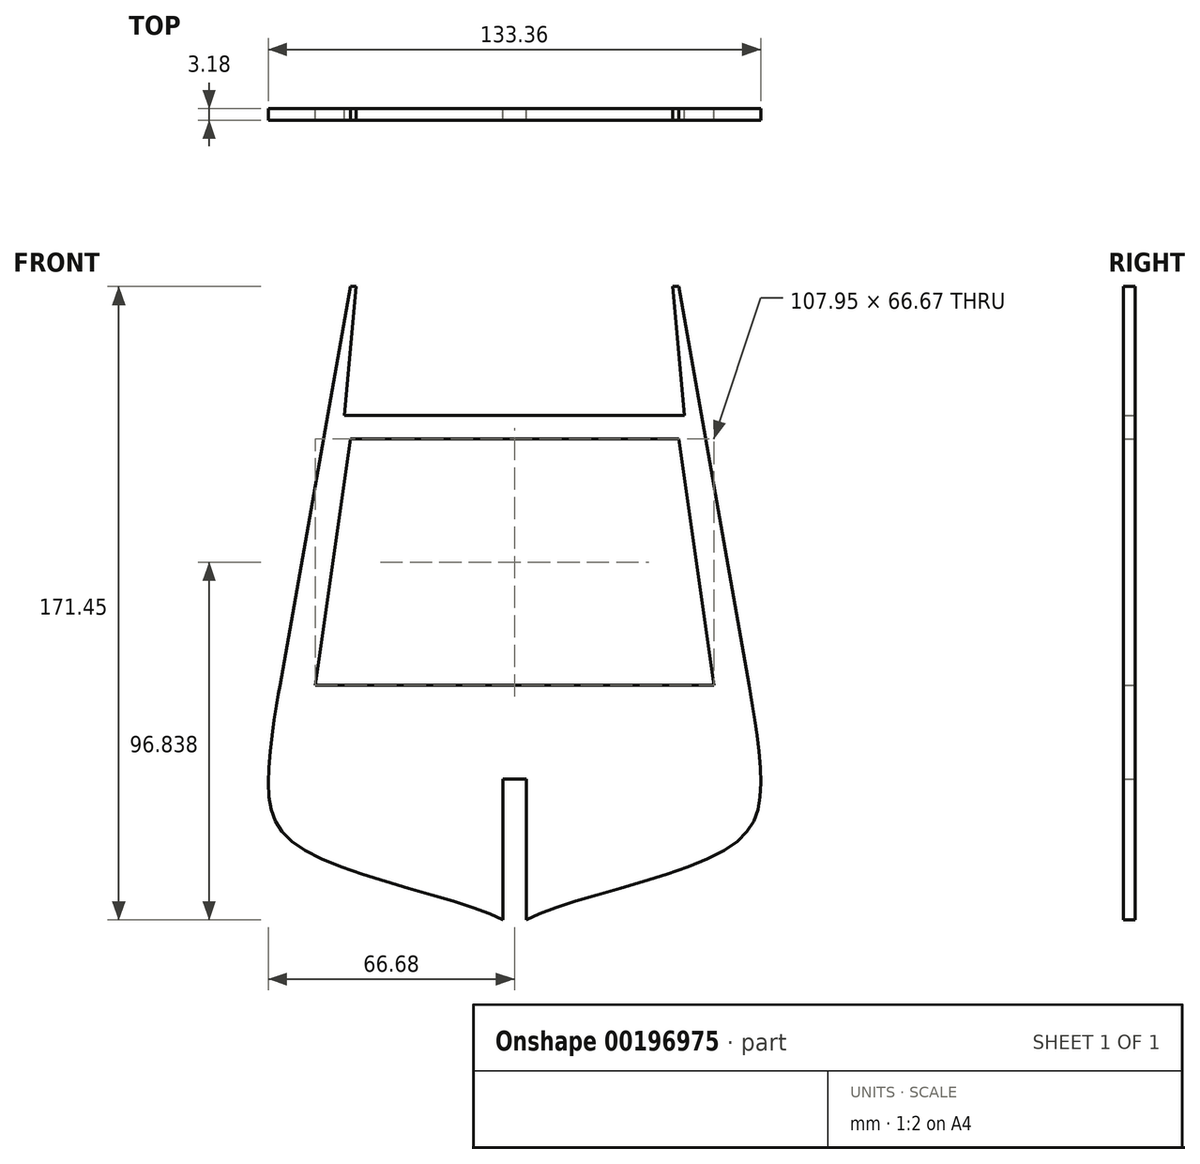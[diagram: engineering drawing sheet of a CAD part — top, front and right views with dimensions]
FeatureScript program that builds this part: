
annotation { "Feature Type Name" : "Feature", "Feature Type Description" : "" }
export const myFeature = defineFeature(function(context is Context, id is Id, definition is map)
    precondition{}
    {
        {
            var Q0;
            Q0=qCreatedBy(makeId("Front.planeOp"),FACE);
            var sketch = newSketch(context, id + "F0", { "sketchPlane" : qUnion([Q0])});
            skLineSegment(sketch, "E0", {"start": v(0, 0) * mm, "end": v(0, 66.68) * mm, "construction": true});
            skLineSegment(sketch, "E1", {"start": v(0, 0) * mm, "end": v(0, -63.5) * mm, "construction": true});
            skLineSegment(sketch, "E2", {"start": v(0, 0) * mm, "end": v(53.97, 0) * mm});
            skLineSegment(sketch, "E3", {"start": v(0, 0) * mm, "end": v(-53.97, 0) * mm});
            skLineSegment(sketch, "E4", {"start": v(53.97, 0) * mm, "end": v(63.5, 0) * mm, "construction": true});
            skLineSegment(sketch, "E5", {"start": v(0, -63.5) * mm, "end": v(3.18, -63.5) * mm, "construction": true});
            skLineSegment(sketch, "E6", {"start": v(0, 66.68) * mm, "end": v(44.45, 66.68) * mm});
            skLineSegment(sketch, "E7", {"start": v(44.45, 66.68) * mm, "end": v(51.73, 66.68) * mm, "construction": true});
            skLineSegment(sketch, "E8", {"start": v(0, 66.68) * mm, "end": v(0, 73.03) * mm, "construction": true});
            skLineSegment(sketch, "E9", {"start": v(0, 73.03) * mm, "end": v(46.04, 73.03) * mm});
            skLineSegment(sketch, "E10", {"start": v(46.04, 73.03) * mm, "end": v(50.61, 73.03) * mm, "construction": true});
            skLineSegment(sketch, "E11", {"start": v(44.45, 66.68) * mm, "end": v(53.97, 0) * mm});
            skLineSegment(sketch, "E12", {"start": v(3.18, -63.5) * mm, "end": v(3.18, -25.4) * mm});
            skLineSegment(sketch, "E13", {"start": v(-3.18, -25.4) * mm, "end": v(-3.18, -63.5) * mm});
            skLineSegment(sketch, "E14", {"start": v(-3.18, -25.4) * mm, "end": v(0, -25.4) * mm});
            skLineSegment(sketch, "E15", {"start": v(0, -25.4) * mm, "end": v(3.18, -25.4) * mm});
            skLineSegment(sketch, "E16", {"start": v(44.45, 107.95) * mm, "end": v(42.86, 107.95) * mm});
            skLineSegment(sketch, "E17", {"start": v(42.86, 107.95) * mm, "end": v(46.04, 73.02) * mm});
            skFitSpline(sketch, "E18", {"points": [v(3.18, -63.5) * mm, v(57.15, -44.45) * mm, v(66.68, -25.4) * mm, v(63.5, 0) * mm], "startDerivative": vector(68.1, 39.32) * mm, "endDerivative": vector(-7.58, 42.97) * mm});
            skLineSegment(sketch, "E19", {"start": v(63.5, 0) * mm, "end": v(44.45, 107.95) * mm});
            skLineSegment(sketch, "E20", {"start": v(3.17, -63.5) * mm, "end": v(13.14, -57.75) * mm, "construction": true});
            skLineSegment(sketch, "E21", {"start": v(3.18, -44.45) * mm, "end": v(57.15, -44.45) * mm, "construction": true});
            skFitSpline(sketch, "E22.MirrorCS", {"points": [v(-3.18, -63.5) * mm, v(-57.15, -44.45) * mm, v(-66.68, -25.4) * mm, v(-63.5, 0) * mm], "startDerivative": vector(-68.1, 39.32) * mm, "endDerivative": vector(7.58, 42.97) * mm});
            skLineSegment(sketch, "E23.MirrorCS", {"start": v(-44.45, 66.68) * mm, "end": v(-53.97, 0) * mm});
            skLineSegment(sketch, "E24.MirrorCS", {"start": v(0, 66.68) * mm, "end": v(-44.45, 66.68) * mm});
            skLineSegment(sketch, "E25.MirrorCS", {"start": v(0, 73.03) * mm, "end": v(-46.04, 73.03) * mm});
            skLineSegment(sketch, "E26.MirrorCS", {"start": v(-63.5, 0) * mm, "end": v(-44.45, 107.95) * mm});
            skLineSegment(sketch, "E27.MirrorCS", {"start": v(-44.45, 107.95) * mm, "end": v(-42.86, 107.95) * mm});
            skLineSegment(sketch, "E28.MirrorCS", {"start": v(-42.86, 107.95) * mm, "end": v(-46.04, 73.02) * mm});
            skSolve(sketch);
        }
        {
            var Q0;
            Q0=makeQuery(id+"F0.imprint","IMPRINT",FACE,{"disambiguationData":[TD([[makeQuery(id+"F0.imprint","IMPRINT",EDGE,{"derivedFrom":sQuery(id+"F0.wireOp",EDGE,"E2")}),-1.0]])]});
            extrude(context, id + "F1", {"entities" : qUnion([Q0]), "endBound" : BoundingType.SYMMETRIC, "depth" : 3.17 * mm});
        }
    });
